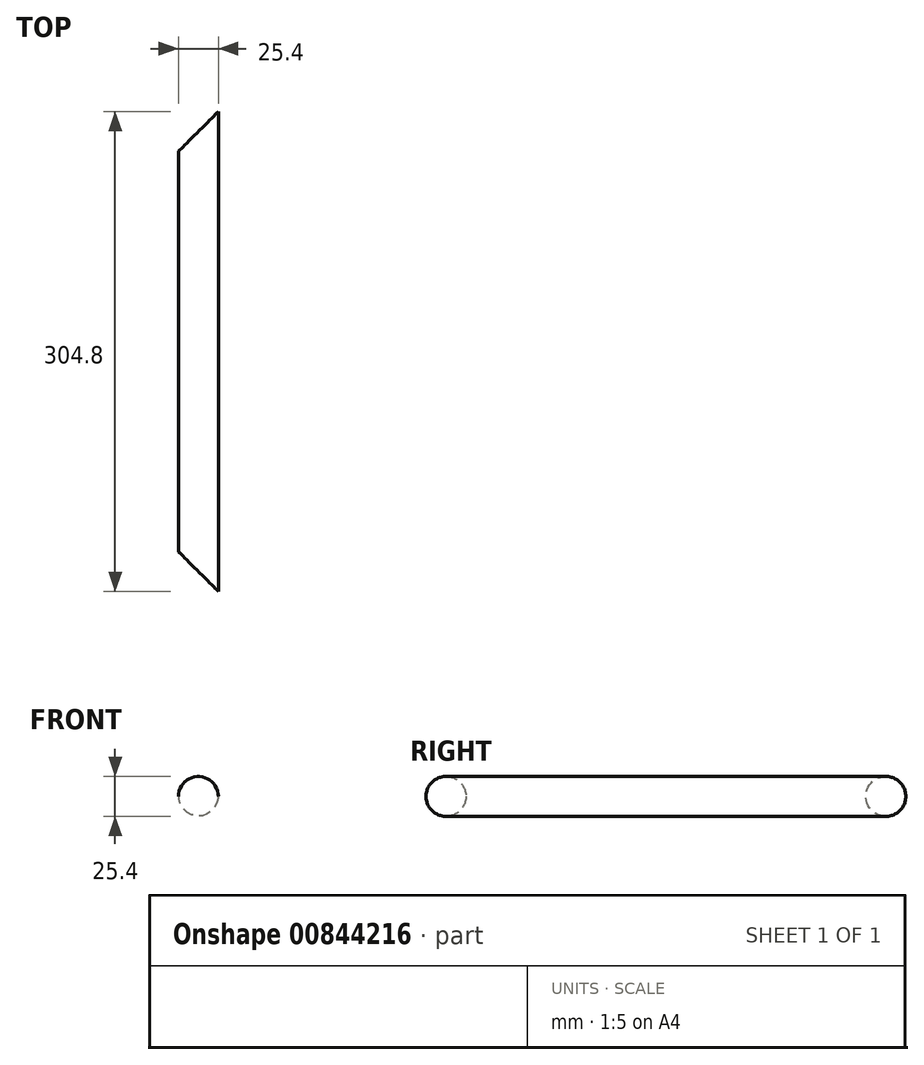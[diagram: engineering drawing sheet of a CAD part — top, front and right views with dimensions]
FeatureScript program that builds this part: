
annotation { "Feature Type Name" : "Feature", "Feature Type Description" : "" }
export const myFeature = defineFeature(function(context is Context, id is Id, definition is map)
    precondition{}
    {
        {
            var Q0;
            Q0=qCreatedBy(makeId("Front.planeOp"),FACE);
            var sketch = newSketch(context, id + "F0", { "sketchPlane" : qUnion([Q0])});
            skCircle(sketch, "E0", {"center": v(0, 0) * mm, "radius": 12.7 * mm});
            skSolve(sketch);
        }
        {
            var Q0;
            Q0 = qSketchRegion(id + "F0", true);
            extrude(context, id + "F1", {"entities" : qUnion([Q0]), "depth" : 304.8 * mm, "offsetDistance" : 25.4 * mm});
        }
        {
            var Q0;
            Q0=qCreatedBy(makeId("Top.planeOp"),FACE);
            var sketch = newSketch(context, id + "F2", { "sketchPlane" : qUnion([Q0])});
            skLineSegment(sketch, "E1", {"start": v(12.7, 0) * mm, "end": v(-12.7, -25.4) * mm});
            skLineSegment(sketch, "E2", {"start": v(-12.7, -25.4) * mm, "end": v(-12.7, 0) * mm});
            skLineSegment(sketch, "E3", {"start": v(-12.7, 0) * mm, "end": v(12.7, 0) * mm});
            skLineSegment(sketch, "E4", {"start": v(12.7, -304.8) * mm, "end": v(-12.7, -304.8) * mm});
            skLineSegment(sketch, "E5", {"start": v(-12.7, -304.8) * mm, "end": v(-12.7, -279.4) * mm});
            skLineSegment(sketch, "E6", {"start": v(-12.7, -279.4) * mm, "end": v(12.7, -304.8) * mm});
            skSolve(sketch);
        }
        {
            var Q0;
            Q0 = qSketchRegion(id + "F2", true);
            extrude(context, id + "F3", {"entities" : qUnion([Q0]), "operationType" : NewBodyOperationType.REMOVE, "endBound" : BoundingType.SYMMETRIC, "oppositeDirection" : true, "depth" : 48.26 * mm, "offsetDistance" : 25.4 * mm});
        }
    });
